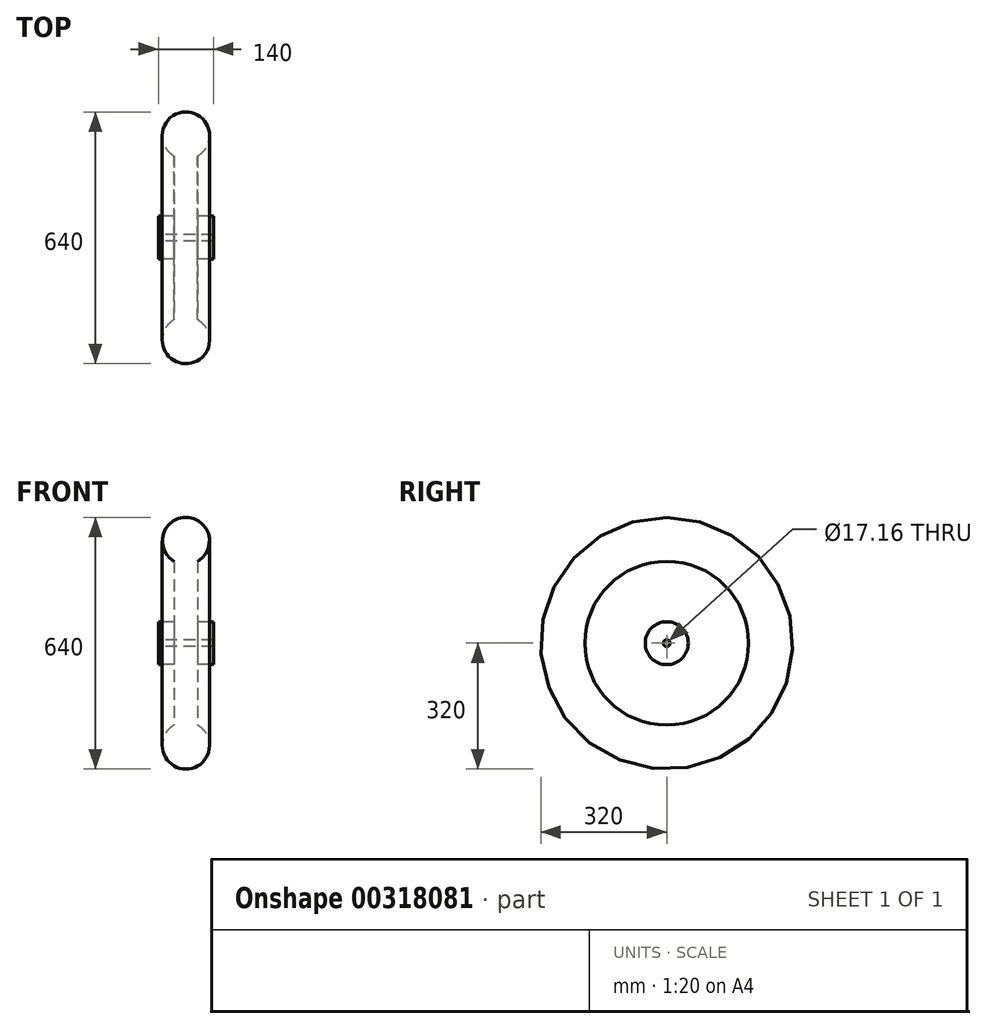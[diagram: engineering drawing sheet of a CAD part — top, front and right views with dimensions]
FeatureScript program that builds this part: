
annotation { "Feature Type Name" : "Feature", "Feature Type Description" : "" }
export const myFeature = defineFeature(function(context is Context, id is Id, definition is map)
    precondition{}
    {
        {
            var Q0;
            Q0=qCreatedBy(makeId("Front.planeOp"),FACE);
            var sketch = newSketch(context, id + "F0", { "sketchPlane" : qUnion([Q0])});
            skPoint(sketch, "E0.third.point", {"position": v(0, 8.58) * mm});
            skLineSegment(sketch, "E1", {"start": v(-70, 8.58) * mm, "end": v(-70, 54.58) * mm});
            skLineSegment(sketch, "E2", {"start": v(-70, 54.58) * mm, "end": v(-30, 54.58) * mm});
            skLineSegment(sketch, "E3", {"start": v(-30, 54.58) * mm, "end": v(-30, 239.6) * mm});
            skCircle(sketch, "E4", {"center": v(0, 260) * mm, "radius": 60 * mm});
            skLineSegment(sketch, "E5.MirrorCS", {"start": v(30, 54.58) * mm, "end": v(30, 239.6) * mm});
            skLineSegment(sketch, "E6.MirrorCS", {"start": v(70, 54.58) * mm, "end": v(30, 54.58) * mm});
            skLineSegment(sketch, "E7.MirrorCS", {"start": v(70, 8.58) * mm, "end": v(70, 54.58) * mm});
            skLineSegment(sketch, "E8", {"start": v(-70, 8.58) * mm, "end": v(70, 8.58) * mm});
            skLineSegment(sketch, "E9", {"start": v(-39.46, 0) * mm, "end": v(39.46, 0) * mm, "construction": true});
            skSolve(sketch);
        }
        {
            var Q0;
            Q0 = qSketchRegion(id + "F0", true);
            var Q1;
            Q1=sQuery(id+"F0.wireOp",EDGE,"E9");
            revolve(context, id + "F1", {"entities" : qUnion([Q0]), "axis" : qUnion([Q1]), "revolveType" : RevolveType.FULL});
        }
        {
            var Q0;
            Q0=makeQuery(id+"F1.opRevolve","SWEPT_FACE",FACE,{"disambiguationData":[OSD([sQuery(id+"F0.wireOp",EDGE,"E3")])]});
            var sketch = newSketch(context, id + "F2", { "sketchPlane" : qUnion([Q0])});
            skArc(sketch, "E10.0", {"start": v(-45.57, 48.54) * mm, "mid": v(0, -66.58) * mm, "end": v(45.57, 48.54) * mm});
            skArc(sketch, "E11.0", {"start": v(-102.63, 167.03) * mm, "mid": v(0, -196.04) * mm, "end": v(102.63, 167.03) * mm});
            skCircle(sketch, "E12.0", {"center": v(0, 0) * mm, "radius": 213.04 * mm});
            skLineSegment(sketch, "E13", {"start": v(0, 66.58) * mm, "end": v(0, 196.04) * mm, "construction": true});
            skCircle(sketch, "E14.cCircle", {"center": v(0, 0) * mm, "radius": 176.62 * mm, "construction": true});
            skLineSegment(sketch, "E14.0", {"start": v(-85.06, 176.62) * mm, "end": v(85.06, 176.62) * mm, "construction": true});
            skLineSegment(sketch, "E14.1", {"start": v(85.06, 176.62) * mm, "end": v(191.12, 43.62) * mm, "construction": true});
            skLineSegment(sketch, "E14.2", {"start": v(191.12, 43.62) * mm, "end": v(153.27, -122.23) * mm, "construction": true});
            skLineSegment(sketch, "E14.3", {"start": v(153.27, -122.23) * mm, "end": v(0, -196.04) * mm, "construction": true});
            skLineSegment(sketch, "E14.4", {"start": v(0, -196.04) * mm, "end": v(-153.27, -122.23) * mm, "construction": true});
            skLineSegment(sketch, "E14.5", {"start": v(-153.27, -122.23) * mm, "end": v(-191.12, 43.62) * mm, "construction": true});
            skLineSegment(sketch, "E14.6", {"start": v(-191.12, 43.62) * mm, "end": v(-85.06, 176.62) * mm, "construction": true});
            skPoint(sketch, "E14.0.midPoint", {"position": v(0, 176.62) * mm});
            skLineSegment(sketch, "E15", {"start": v(-85.06, 176.62) * mm, "end": v(-28.89, 59.99) * mm, "construction": true});
            skLineSegment(sketch, "E16", {"start": v(85.06, 176.62) * mm, "end": v(28.89, 59.99) * mm, "construction": true});
            skLineSegment(sketch, "E17", {"start": v(-61.64, 174.1) * mm, "end": v(-12.55, 72.16) * mm});
            skLineSegment(sketch, "E18", {"start": v(-102.63, 167.03) * mm, "end": v(-45.57, 48.54) * mm});
            skLineSegment(sketch, "E19.MirrorCS", {"start": v(102.63, 167.03) * mm, "end": v(45.57, 48.54) * mm});
            skLineSegment(sketch, "E20.MirrorCS", {"start": v(61.64, 174.1) * mm, "end": v(12.55, 72.16) * mm});
            skLineSegment(sketch, "E21", {"start": v(65.16, 13.7) * mm, "end": v(228.34, -3.04) * mm, "construction": true});
            skPoint(sketch, "E22.visualSharp", {"position": v(-66.6, 184.38) * mm});
            skArc(sketch, "E22.filletArc", {"start": v(-55.46, 188.03) * mm, "mid": v(-61.77, 182.5) * mm, "end": v(-61.64, 174.1) * mm});
            skArc(sketch, "E23.trimOffspring", {"start": v(55.46, 188.03) * mm, "mid": v(0, 196.04) * mm, "end": v(-55.46, 188.03) * mm});
            skPoint(sketch, "E24.visualSharp", {"position": v(66.6, 184.38) * mm});
            skArc(sketch, "E24.filletArc", {"start": v(61.64, 174.1) * mm, "mid": v(61.77, 182.5) * mm, "end": v(55.46, 188.03) * mm});
            skArc(sketch, "E25.trimOffspring", {"start": v(3.08, 66.5) * mm, "mid": v(0, 66.58) * mm, "end": v(-3.08, 66.5) * mm});
            skPoint(sketch, "E26.visualSharp", {"position": v(9.53, 65.9) * mm});
            skArc(sketch, "E26.filletArc", {"start": v(3.08, 66.5) * mm, "mid": v(8.67, 67.91) * mm, "end": v(12.55, 72.16) * mm});
            skPoint(sketch, "E27.visualSharp", {"position": v(-9.53, 65.9) * mm});
            skArc(sketch, "E27.filletArc", {"start": v(-12.55, 72.16) * mm, "mid": v(-8.67, 67.91) * mm, "end": v(-3.08, 66.5) * mm});
            skSolve(sketch);
        }
        {
            var Q0;
            Q0=makeQuery(id+"F2.imprint","IMPRINT",FACE,{"disambiguationData":[TD([[makeQuery(id+"F2.imprint","IMPRINT",EDGE,{"derivedFrom":sQuery(id+"F2.wireOp",EDGE,"E17")}),1.0]])]});
            extrude(context, id + "F3", {"entities" : qUnion([Q0]), "operationType" : NewBodyOperationType.ADD, "oppositeDirection" : true, "depth" : 25 * mm});
        }
    });
